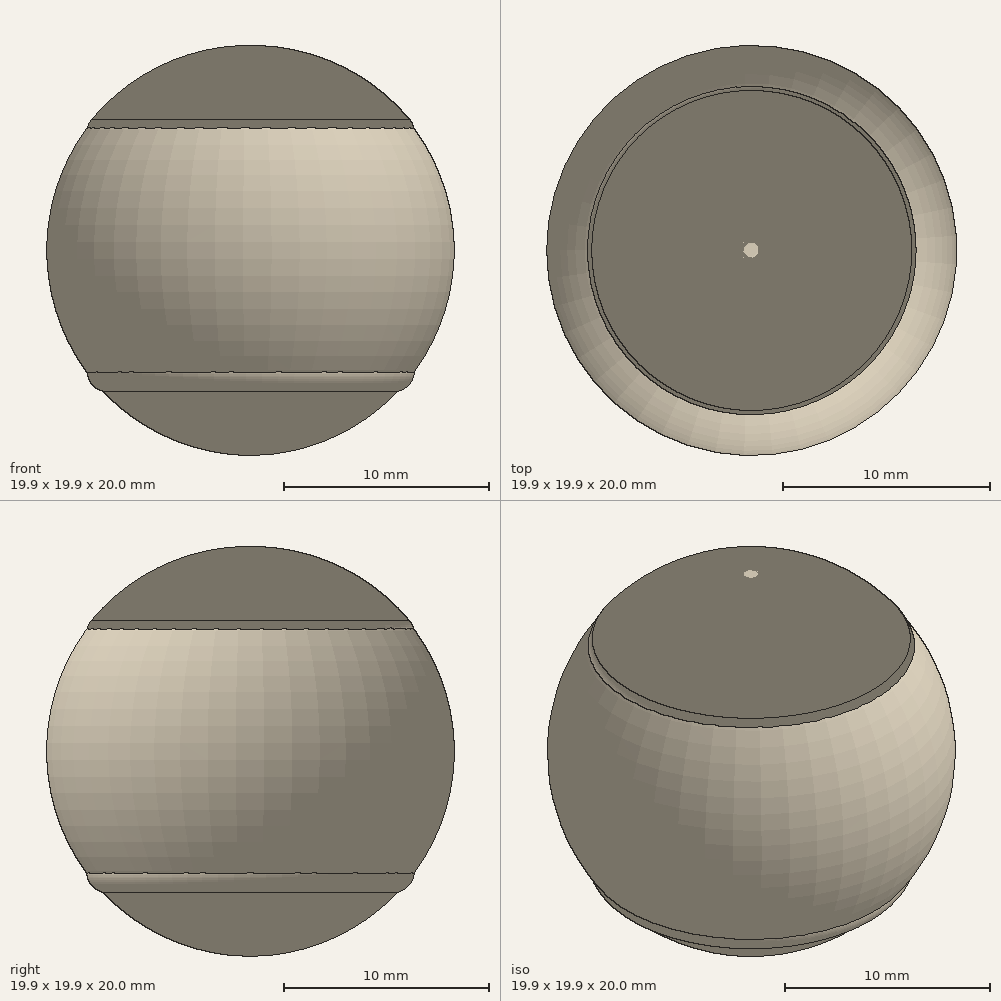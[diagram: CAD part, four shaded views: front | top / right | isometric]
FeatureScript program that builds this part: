
annotation { "Feature Type Name" : "Feature", "Feature Type Description" : "" }
export const myFeature = defineFeature(function(context is Context, id is Id, definition is map)
    precondition{}
    {
        {
            var Q0;
            Q0=qCreatedBy(makeId("Top.planeOp"),FACE);
            var sketch = newSketch(context, id + "F0", { "sketchPlane" : qUnion([Q0])});
            skArc(sketch, "E0", {"start": v(-2.7, 1.49) * mm, "mid": v(0, -3.08) * mm, "end": v(2.7, 1.49) * mm});
            skCircle(sketch, "E1", {"center": v(0, 0) * mm, "radius": 8 * mm});
            skCircle(sketch, "E2", {"center": v(0, 0) * mm, "radius": 3.07 * mm});
            skSolve(sketch);
        }
        {
            var Q0;
            Q0=makeQuery(id+"F0.imprint","IMPRINT",FACE,{"disambiguationData":[TD([[makeQuery(id+"F0.imprint","IMPRINT",EDGE,{"derivedFrom":sQuery(id+"F0.wireOp",EDGE,"E1")}),1.0]])]});
            extrude(context, id + "F1", {"entities" : qUnion([Q0]), "depth" : 6 * mm});
        }
        {
            var Q0;
            Q0=qCreatedBy(makeId("Front.planeOp"),FACE);
            var sketch = newSketch(context, id + "F2", { "sketchPlane" : qUnion([Q0])});
            skLineSegment(sketch, "E3.left", {"start": v(-7.37, 2) * mm, "end": v(-7.37, 11.68) * mm});
            skLineSegment(sketch, "E3.right", {"start": v(-8.62, 2) * mm, "end": v(-8.62, 11.68) * mm});
            skArc(sketch, "E4", {"start": v(-8.62, 2) * mm, "mid": v(-8, 1.37) * mm, "end": v(-7.38, 2) * mm});
            skArc(sketch, "E5", {"start": v(-7.37, 11.68) * mm, "mid": v(-8, 12.3) * mm, "end": v(-8.62, 11.68) * mm});
            skSolve(sketch);
        }
        {
            var Q0;
            Q0=makeQuery(id+"F2.imprint","IMPRINT",FACE,{"disambiguationData":[TD([[makeQuery(id+"F2.imprint","IMPRINT",EDGE,{"derivedFrom":sQuery(id+"F2.wireOp",EDGE,"E3.left")}),1.0]])]});
            var Q1;
            Q1=sQuery(id+"F2.wireOp",EDGE,"E3.left");
            revolve(context, id + "F3", {"entities" : qUnion([Q0]), "axis" : qUnion([Q1]), "revolveType" : RevolveType.FULL});
        }
        {
            var Q0;
            Q0=makeQuery(id+"F1.opExtrude","CAP_EDGE",EDGE,{"disambiguationData":[OSD([sQuery(id+"F0.wireOp",EDGE,"E2")])],"isStart":true});
            var Q1;
            Q1=makeQuery(id+"F1.opExtrude","CAP_EDGE",EDGE,{"disambiguationData":[OSD([sQuery(id+"F0.wireOp",EDGE,"E1")])],"isStart":true});
            fillet(context, id + "F4", {"entities" : qUnion([Q0, Q1]), "radius" : 1 * mm, "tangentPropagation" : true, "allowEdgeOverflow" : false});
        }
        {
            var Q0;
            Q0=makeQuery(id+"F3.opRevolve","SWEPT_BODY",BODY,{"disambiguationData":[OSD([sQuery(id+"F2.wireOp",EDGE,"E3.left"),sQuery(id+"F2.wireOp",EDGE,"E3.right"),sQuery(id+"F2.wireOp",EDGE,"E4"),sQuery(id+"F2.wireOp",EDGE,"E5")])]});
            var Q1;
            Q1=makeQuery(id+"F1.opExtrude","SWEPT_FACE",FACE,{"disambiguationData":[OSD([sQuery(id+"F0.wireOp",EDGE,"E1")])]});
            circularPattern(context, id + "F5", {"entities" : qUnion([Q0]), "axis" : qUnion([Q1]), "angle" : 24 * degree, "instanceCount" : 15});
        }
        {
            var Q0;
            Q0=makeQuery(id+"F1.opExtrude","CAP_FACE",FACE,{"disambiguationData":[OSD([sQuery(id+"F0.wireOp",EDGE,"E1"),sQuery(id+"F0.wireOp",EDGE,"E2")])],"isStart":false});
            var sketch = newSketch(context, id + "F6", { "sketchPlane" : qUnion([Q0])});
            skCircle(sketch, "E6", {"center": v(0, 0) * mm, "radius": 8 * mm});
            skArc(sketch, "E7", {"start": v(-1.98, 2.36) * mm, "mid": v(-3.08, 0) * mm, "end": v(-1.98, -2.36) * mm});
            skLineSegment(sketch, "E8", {"start": v(-1.98, -2.36) * mm, "end": v(-1.98, 2.36) * mm});
            skSolve(sketch);
        }
        {
            var Q0;
            Q0=makeQuery(id+"F6.imprint","IMPRINT",FACE,{"disambiguationData":[TD([[makeQuery(id+"F6.imprint","IMPRINT",EDGE,{"derivedFrom":sQuery(id+"F6.wireOp",EDGE,"E7")}),-1.0]])]});
            var Q1;
            Q1=makeQuery(id+"F6.imprint","IMPRINT",FACE,{"disambiguationData":[TD([[makeQuery(id+"F6.imprint","IMPRINT",EDGE,{"disambiguationData":[OD(0.0)],"derivedFrom":sQuery(id+"F6.wireOp",EDGE,"E6")}),1.0]])]});
            var Q2;
            Q2=makeQuery(id+"F6.imprint","IMPRINT",FACE,{"disambiguationData":[TD([[makeQuery(id+"F6.imprint","IMPRINT",EDGE,{"disambiguationData":[OD(1.0)],"derivedFrom":sQuery(id+"F6.wireOp",EDGE,"E6")}),-1.0]])]});
            var Q3;
            {var subQ0=sQuery(id+"F6.wireOp",EDGE,"157f1673-d0b7-42ae-b503-b637a08b7d80");var subQ3=sQuery(id+"F6.wireOp",EDGE,"E7");var subQ4=makeQuery(id+"F6.imprint","INTERSECT",VERTEX,{"derivedFrom":[subQ3,subQ0]});Q3=makeQuery(id+"F6.imprint","IMPRINT",FACE,{"disambiguationData":[TD([[makeQuery(id+"F6.imprint","IMPRINT",EDGE,{"disambiguationData":[TD([[subQ4,-1.0]])],"derivedFrom":subQ0}),1.0]])]});}
            var Q4;
            {var subQ0=sQuery(id+"F6.wireOp",EDGE,"157f1673-d0b7-42ae-b503-b637a08b7d80");var subQ3=sQuery(id+"F6.wireOp",EDGE,"E7");var subQ4=makeQuery(id+"F6.imprint","INTERSECT",VERTEX,{"derivedFrom":[subQ3,subQ0]});Q4=makeQuery(id+"F6.imprint","IMPRINT",FACE,{"disambiguationData":[TD([[makeQuery(id+"F6.imprint","IMPRINT",EDGE,{"disambiguationData":[TD([[subQ4,-1.0]])],"derivedFrom":subQ0}),-1.0]])]});}
            var Q5;
            Q5=makeQuery(id+"F6.imprint","IMPRINT",FACE,{"disambiguationData":[TD([[makeQuery(id+"F6.imprint","IMPRINT",EDGE,{"derivedFrom":sQuery(id+"F6.wireOp",EDGE,"E7")}),1.0]])]});
            extrude(context, id + "F7", {"entities" : qUnion([Q0, Q1, Q2, Q3, Q4, Q5]), "depth" : 7 * mm});
        }
        {
            var Q0;
            Q0=qCreatedBy(makeId("Right.planeOp"),FACE);
            var sketch = newSketch(context, id + "F8", { "sketchPlane" : qUnion([Q0])});
            skArc(sketch, "E9", {"start": v(-8, 13) * mm, "mid": v(-4.46, 10.1) * mm, "end": v(0, 9.08) * mm});
            skLineSegment(sketch, "E10", {"start": v(0, 13) * mm, "end": v(0, 9.08) * mm});
            skLineSegment(sketch, "E11", {"start": v(0, 13) * mm, "end": v(-8, 13) * mm});
            skArc(sketch, "E12.0.MirrorCS", {"start": v(-8, 13) * mm, "mid": v(-4.46, 15.9) * mm, "end": v(0, 16.92) * mm});
            skLineSegment(sketch, "E13", {"start": v(0, 25.01) * mm, "end": v(0, 5.17) * mm});
            skSolve(sketch);
        }
        {
            var Q0;
            {var subQ2=sQuery(id+"F8.wireOp",EDGE,"E11");Q0=makeQuery(id+"F8.imprint","IMPRINT",FACE,{"disambiguationData":[TD([[makeQuery(id+"F8.imprint","IMPRINT",EDGE,{"derivedFrom":subQ2}),-1.0]])]});}
            var Q1;
            Q1=sQuery(id+"F8.wireOp",EDGE,"E10");
            revolve(context, id + "F9", {"operationType" : NewBodyOperationType.ADD, "entities" : qUnion([Q0]), "axis" : qUnion([Q1]), "revolveType" : RevolveType.FULL});
        }
        {
            var Q0;
            Q0=makeQuery(id+"F9.boolean.opBoolean","MERGE",EDGE,{"derivedFrom":[makeQuery(id+"F7.opExtrude","CAP_EDGE",EDGE,{"disambiguationData":[OSD([sQuery(id+"F6.wireOp",EDGE,"E6")])],"isStart":false}),makeQuery(id+"F9.opRevolve","SWEPT_EDGE",EDGE,{"disambiguationData":[OSD([sQuery(id+"F8.wireOp",EDGE,"E9"),sQuery(id+"F8.wireOp",EDGE,"E11")])]})]});
            fillet(context, id + "F10", {"entities" : qUnion([Q0]), "radius" : 1 * mm, "tangentPropagation" : true, "allowEdgeOverflow" : false});
        }
    });
